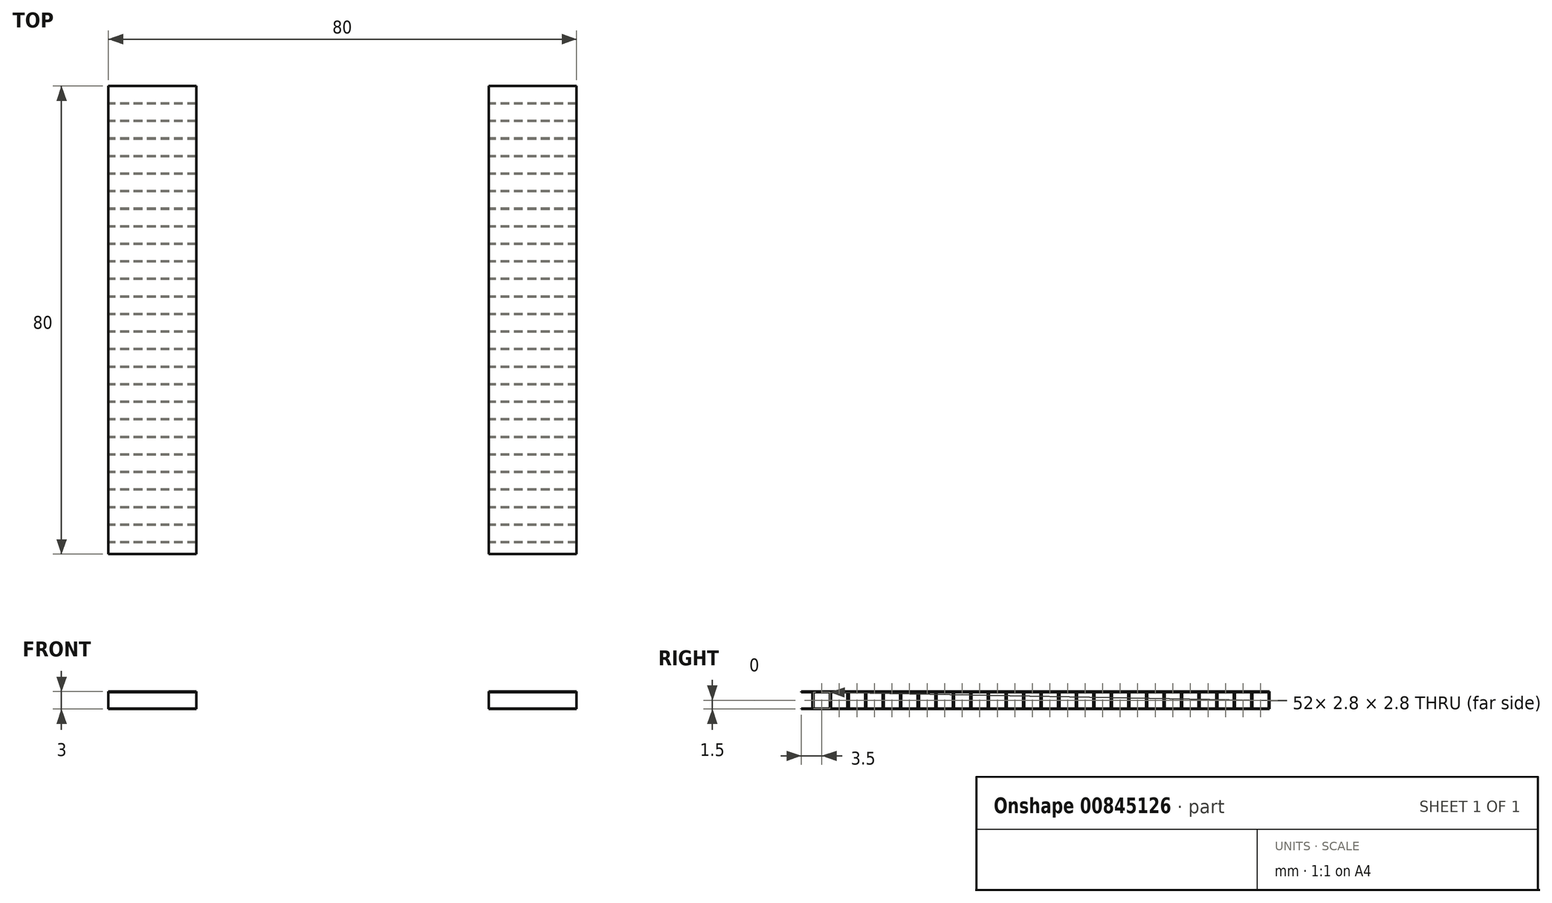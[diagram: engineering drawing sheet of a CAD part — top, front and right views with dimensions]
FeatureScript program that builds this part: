
annotation { "Feature Type Name" : "Feature", "Feature Type Description" : "" }
export const myFeature = defineFeature(function(context is Context, id is Id, definition is map)
    precondition{}
    {
        {
            var Q0;
            Q0=qCreatedBy(makeId("Top.planeOp"),FACE);
            var sketch = newSketch(context, id + "F0", { "sketchPlane" : qUnion([Q0])});
            skLineSegment(sketch, "E0.bottom", {"start": v(40, 40) * mm, "end": v(-40, 40) * mm});
            skLineSegment(sketch, "E0.top", {"start": v(40, -40) * mm, "end": v(-40, -40) * mm});
            skLineSegment(sketch, "E0.left", {"start": v(40, 40) * mm, "end": v(40, -40) * mm});
            skLineSegment(sketch, "E0.right", {"start": v(-40, 40) * mm, "end": v(-40, -40) * mm});
            skPoint(sketch, "E0.middle", {"position": v(0, 0) * mm});
            skLineSegment(sketch, "E1.bottom", {"start": v(-25, 40) * mm, "end": v(25, 40) * mm});
            skLineSegment(sketch, "E1.top", {"start": v(-25, -40) * mm, "end": v(25, -40) * mm});
            skLineSegment(sketch, "E1.left", {"start": v(-25, 40) * mm, "end": v(-25, -40) * mm});
            skLineSegment(sketch, "E1.right", {"start": v(25, 40) * mm, "end": v(25, -40) * mm});
            skSolve(sketch);
        }
        {
            var Q0;
            {var subQ0=sQuery(id+"F0.wireOp",EDGE,"E0.left");Q0=makeQuery(id+"F0.imprint","IMPRINT",FACE,{"disambiguationData":[TD([[makeQuery(id+"F0.imprint","IMPRINT",EDGE,{"derivedFrom":subQ0}),-1.0]])]});}
            var Q1;
            {var subQ0=sQuery(id+"F0.wireOp",EDGE,"E0.right");Q1=makeQuery(id+"F0.imprint","IMPRINT",FACE,{"disambiguationData":[TD([[makeQuery(id+"F0.imprint","IMPRINT",EDGE,{"derivedFrom":subQ0}),1.0]])]});}
            extrude(context, id + "F1", {"entities" : qUnion([Q0, Q1]), "depth" : 3 * mm, "offsetDistance" : 25 * mm});
        }
        {
            var Q0;
            Q0=makeQuery(id+"F1.opExtrude","SWEPT_FACE",FACE,{"disambiguationData":[OSD([sQuery(id+"F0.wireOp",EDGE,"E0.right")])]});
            var sketch = newSketch(context, id + "F2", { "sketchPlane" : qUnion([Q0])});
            skLineSegment(sketch, "E2.bottom", {"start": v(-39.9, 2.9) * mm, "end": v(39.9, 2.9) * mm});
            skLineSegment(sketch, "E2.top", {"start": v(-39.9, 0.1) * mm, "end": v(39.9, 0.1) * mm});
            skLineSegment(sketch, "E2.left", {"start": v(-39.9, 2.9) * mm, "end": v(-39.9, 0.1) * mm});
            skLineSegment(sketch, "E3", {"start": v(-37.1, 2.9) * mm, "end": v(-37.1, 0.1) * mm});
            skLineSegment(sketch, "E4.1.0.0", {"start": v(-36.9, 2.9) * mm, "end": v(-36.9, 0.1) * mm});
            skLineSegment(sketch, "E4.1.0.1", {"start": v(-34.1, 2.9) * mm, "end": v(-34.1, 0.1) * mm});
            skLineSegment(sketch, "E4.2.0.0", {"start": v(-33.9, 2.9) * mm, "end": v(-33.9, 0.1) * mm});
            skLineSegment(sketch, "E4.2.0.1", {"start": v(-31.1, 2.9) * mm, "end": v(-31.1, 0.1) * mm});
            skLineSegment(sketch, "E4.3.0.0", {"start": v(-30.9, 2.9) * mm, "end": v(-30.9, 0.1) * mm});
            skLineSegment(sketch, "E4.3.0.1", {"start": v(-28.1, 2.9) * mm, "end": v(-28.1, 0.1) * mm});
            skLineSegment(sketch, "E4.4.0.0", {"start": v(-27.9, 2.9) * mm, "end": v(-27.9, 0.1) * mm});
            skLineSegment(sketch, "E4.4.0.1", {"start": v(-25.1, 2.9) * mm, "end": v(-25.1, 0.1) * mm});
            skLineSegment(sketch, "E4.5.0.0", {"start": v(-24.9, 2.9) * mm, "end": v(-24.9, 0.1) * mm});
            skLineSegment(sketch, "E4.5.0.1", {"start": v(-22.1, 2.9) * mm, "end": v(-22.1, 0.1) * mm});
            skLineSegment(sketch, "E4.6.0.0", {"start": v(-21.9, 2.9) * mm, "end": v(-21.9, 0.1) * mm});
            skLineSegment(sketch, "E4.6.0.1", {"start": v(-19.1, 2.9) * mm, "end": v(-19.1, 0.1) * mm});
            skLineSegment(sketch, "E4.7.0.0", {"start": v(-18.9, 2.9) * mm, "end": v(-18.9, 0.1) * mm});
            skLineSegment(sketch, "E4.7.0.1", {"start": v(-16.1, 2.9) * mm, "end": v(-16.1, 0.1) * mm});
            skLineSegment(sketch, "E4.8.0.0", {"start": v(-15.9, 2.9) * mm, "end": v(-15.9, 0.1) * mm});
            skLineSegment(sketch, "E4.8.0.1", {"start": v(-13.1, 2.9) * mm, "end": v(-13.1, 0.1) * mm});
            skLineSegment(sketch, "E4.9.0.0", {"start": v(-12.9, 2.9) * mm, "end": v(-12.9, 0.1) * mm});
            skLineSegment(sketch, "E4.9.0.1", {"start": v(-10.1, 2.9) * mm, "end": v(-10.1, 0.1) * mm});
            skLineSegment(sketch, "E4.10.0.0", {"start": v(-9.9, 2.9) * mm, "end": v(-9.9, 0.1) * mm});
            skLineSegment(sketch, "E4.10.0.1", {"start": v(-7.1, 2.9) * mm, "end": v(-7.1, 0.1) * mm});
            skLineSegment(sketch, "E4.11.0.0", {"start": v(-6.9, 2.9) * mm, "end": v(-6.9, 0.1) * mm});
            skLineSegment(sketch, "E4.11.0.1", {"start": v(-4.1, 2.9) * mm, "end": v(-4.1, 0.1) * mm});
            skLineSegment(sketch, "E4.12.0.0", {"start": v(-3.9, 2.9) * mm, "end": v(-3.9, 0.1) * mm});
            skLineSegment(sketch, "E4.12.0.1", {"start": v(-1.1, 2.9) * mm, "end": v(-1.1, 0.1) * mm});
            skLineSegment(sketch, "E4.13.0.0", {"start": v(-0.9, 2.9) * mm, "end": v(-0.9, 0.1) * mm});
            skLineSegment(sketch, "E4.13.0.1", {"start": v(1.9, 2.9) * mm, "end": v(1.9, 0.1) * mm});
            skLineSegment(sketch, "E4.14.0.0", {"start": v(2.1, 2.9) * mm, "end": v(2.1, 0.1) * mm});
            skLineSegment(sketch, "E4.14.0.1", {"start": v(4.9, 2.9) * mm, "end": v(4.9, 0.1) * mm});
            skLineSegment(sketch, "E4.15.0.0", {"start": v(5.1, 2.9) * mm, "end": v(5.1, 0.1) * mm});
            skLineSegment(sketch, "E4.15.0.1", {"start": v(7.9, 2.9) * mm, "end": v(7.9, 0.1) * mm});
            skLineSegment(sketch, "E4.16.0.0", {"start": v(8.1, 2.9) * mm, "end": v(8.1, 0.1) * mm});
            skLineSegment(sketch, "E4.16.0.1", {"start": v(10.9, 2.9) * mm, "end": v(10.9, 0.1) * mm});
            skLineSegment(sketch, "E4.17.0.0", {"start": v(11.1, 2.9) * mm, "end": v(11.1, 0.1) * mm});
            skLineSegment(sketch, "E4.17.0.1", {"start": v(13.9, 2.9) * mm, "end": v(13.9, 0.1) * mm});
            skLineSegment(sketch, "E4.18.0.0", {"start": v(14.1, 2.9) * mm, "end": v(14.1, 0.1) * mm});
            skLineSegment(sketch, "E4.18.0.1", {"start": v(16.9, 2.9) * mm, "end": v(16.9, 0.1) * mm});
            skLineSegment(sketch, "E4.19.0.0", {"start": v(17.1, 2.9) * mm, "end": v(17.1, 0.1) * mm});
            skLineSegment(sketch, "E4.19.0.1", {"start": v(19.9, 2.9) * mm, "end": v(19.9, 0.1) * mm});
            skLineSegment(sketch, "E4.20.0.0", {"start": v(20.1, 2.9) * mm, "end": v(20.1, 0.1) * mm});
            skLineSegment(sketch, "E4.20.0.1", {"start": v(22.9, 2.9) * mm, "end": v(22.9, 0.1) * mm});
            skLineSegment(sketch, "E4.21.0.0", {"start": v(23.1, 2.9) * mm, "end": v(23.1, 0.1) * mm});
            skLineSegment(sketch, "E4.21.0.1", {"start": v(25.9, 2.9) * mm, "end": v(25.9, 0.1) * mm});
            skLineSegment(sketch, "E4.22.0.0", {"start": v(26.1, 2.9) * mm, "end": v(26.1, 0.1) * mm});
            skLineSegment(sketch, "E4.22.0.1", {"start": v(28.9, 2.9) * mm, "end": v(28.9, 0.1) * mm});
            skLineSegment(sketch, "E4.23.0.0", {"start": v(29.1, 2.9) * mm, "end": v(29.1, 0.1) * mm});
            skLineSegment(sketch, "E4.23.0.1", {"start": v(31.9, 2.9) * mm, "end": v(31.9, 0.1) * mm});
            skLineSegment(sketch, "E4.24.0.0", {"start": v(32.1, 2.9) * mm, "end": v(32.1, 0.1) * mm});
            skLineSegment(sketch, "E4.24.0.1", {"start": v(34.9, 2.9) * mm, "end": v(34.9, 0.1) * mm});
            skLineSegment(sketch, "E4.25.0.0", {"start": v(35.1, 2.9) * mm, "end": v(35.1, 0.1) * mm});
            skLineSegment(sketch, "E4.25.0.1", {"start": v(37.9, 2.9) * mm, "end": v(37.9, 0.1) * mm});
            skLineSegment(sketch, "E4.26.0.0", {"start": v(38.1, 2.9) * mm, "end": v(38.1, 0.1) * mm});
            skLineSegment(sketch, "E4.26.0.1", {"start": v(40.9, 2.9) * mm, "end": v(40.9, 0.1) * mm});
            skLineSegment(sketch, "E4.direction1", {"start": v(-39.9, 0.1) * mm, "end": v(-36.9, 0.1) * mm, "construction": true});
            skLineSegment(sketch, "E5", {"start": v(39.9, 2.9) * mm, "end": v(40.9, 2.9) * mm});
            skLineSegment(sketch, "E6", {"start": v(39.9, 0.1) * mm, "end": v(40.9, 0.1) * mm});
            skSolve(sketch);
        }
        {
            var Q0;
            {var subQ0=sQuery(id+"F2.wireOp",EDGE,"E4.1.0.0");Q0=makeQuery(id+"F2.imprint","IMPRINT",FACE,{"disambiguationData":[TD([[makeQuery(id+"F2.imprint","IMPRINT",EDGE,{"derivedFrom":subQ0}),1.0]])]});}
            var Q1;
            {var subQ0=sQuery(id+"F2.wireOp",EDGE,"E4.2.0.0");Q1=makeQuery(id+"F2.imprint","IMPRINT",FACE,{"disambiguationData":[TD([[makeQuery(id+"F2.imprint","IMPRINT",EDGE,{"derivedFrom":subQ0}),1.0]])]});}
            var Q2;
            {var subQ0=sQuery(id+"F2.wireOp",EDGE,"E4.3.0.0");Q2=makeQuery(id+"F2.imprint","IMPRINT",FACE,{"disambiguationData":[TD([[makeQuery(id+"F2.imprint","IMPRINT",EDGE,{"derivedFrom":subQ0}),1.0]])]});}
            var Q3;
            {var subQ0=sQuery(id+"F2.wireOp",EDGE,"E4.4.0.0");Q3=makeQuery(id+"F2.imprint","IMPRINT",FACE,{"disambiguationData":[TD([[makeQuery(id+"F2.imprint","IMPRINT",EDGE,{"derivedFrom":subQ0}),1.0]])]});}
            var Q4;
            {var subQ0=sQuery(id+"F2.wireOp",EDGE,"E4.5.0.0");Q4=makeQuery(id+"F2.imprint","IMPRINT",FACE,{"disambiguationData":[TD([[makeQuery(id+"F2.imprint","IMPRINT",EDGE,{"derivedFrom":subQ0}),1.0]])]});}
            var Q5;
            {var subQ0=sQuery(id+"F2.wireOp",EDGE,"E4.6.0.0");Q5=makeQuery(id+"F2.imprint","IMPRINT",FACE,{"disambiguationData":[TD([[makeQuery(id+"F2.imprint","IMPRINT",EDGE,{"derivedFrom":subQ0}),1.0]])]});}
            var Q6;
            {var subQ0=sQuery(id+"F2.wireOp",EDGE,"E4.7.0.0");Q6=makeQuery(id+"F2.imprint","IMPRINT",FACE,{"disambiguationData":[TD([[makeQuery(id+"F2.imprint","IMPRINT",EDGE,{"derivedFrom":subQ0}),1.0]])]});}
            var Q7;
            {var subQ0=sQuery(id+"F2.wireOp",EDGE,"E4.8.0.0");Q7=makeQuery(id+"F2.imprint","IMPRINT",FACE,{"disambiguationData":[TD([[makeQuery(id+"F2.imprint","IMPRINT",EDGE,{"derivedFrom":subQ0}),1.0]])]});}
            var Q8;
            {var subQ0=sQuery(id+"F2.wireOp",EDGE,"E4.9.0.0");Q8=makeQuery(id+"F2.imprint","IMPRINT",FACE,{"disambiguationData":[TD([[makeQuery(id+"F2.imprint","IMPRINT",EDGE,{"derivedFrom":subQ0}),1.0]])]});}
            var Q9;
            {var subQ0=sQuery(id+"F2.wireOp",EDGE,"E4.10.0.0");Q9=makeQuery(id+"F2.imprint","IMPRINT",FACE,{"disambiguationData":[TD([[makeQuery(id+"F2.imprint","IMPRINT",EDGE,{"derivedFrom":subQ0}),1.0]])]});}
            var Q10;
            {var subQ0=sQuery(id+"F2.wireOp",EDGE,"E4.11.0.0");Q10=makeQuery(id+"F2.imprint","IMPRINT",FACE,{"disambiguationData":[TD([[makeQuery(id+"F2.imprint","IMPRINT",EDGE,{"derivedFrom":subQ0}),1.0]])]});}
            var Q11;
            {var subQ0=sQuery(id+"F2.wireOp",EDGE,"E4.12.0.0");Q11=makeQuery(id+"F2.imprint","IMPRINT",FACE,{"disambiguationData":[TD([[makeQuery(id+"F2.imprint","IMPRINT",EDGE,{"derivedFrom":subQ0}),1.0]])]});}
            var Q12;
            {var subQ0=sQuery(id+"F2.wireOp",EDGE,"E4.13.0.0");Q12=makeQuery(id+"F2.imprint","IMPRINT",FACE,{"disambiguationData":[TD([[makeQuery(id+"F2.imprint","IMPRINT",EDGE,{"derivedFrom":subQ0}),1.0]])]});}
            var Q13;
            {var subQ0=sQuery(id+"F2.wireOp",EDGE,"E4.14.0.0");Q13=makeQuery(id+"F2.imprint","IMPRINT",FACE,{"disambiguationData":[TD([[makeQuery(id+"F2.imprint","IMPRINT",EDGE,{"derivedFrom":subQ0}),1.0]])]});}
            var Q14;
            {var subQ0=sQuery(id+"F2.wireOp",EDGE,"E4.15.0.0");Q14=makeQuery(id+"F2.imprint","IMPRINT",FACE,{"disambiguationData":[TD([[makeQuery(id+"F2.imprint","IMPRINT",EDGE,{"derivedFrom":subQ0}),1.0]])]});}
            var Q15;
            {var subQ0=sQuery(id+"F2.wireOp",EDGE,"E4.17.0.0");Q15=makeQuery(id+"F2.imprint","IMPRINT",FACE,{"disambiguationData":[TD([[makeQuery(id+"F2.imprint","IMPRINT",EDGE,{"derivedFrom":subQ0}),1.0]])]});}
            var Q16;
            {var subQ0=sQuery(id+"F2.wireOp",EDGE,"E4.18.0.0");Q16=makeQuery(id+"F2.imprint","IMPRINT",FACE,{"disambiguationData":[TD([[makeQuery(id+"F2.imprint","IMPRINT",EDGE,{"derivedFrom":subQ0}),1.0]])]});}
            var Q17;
            {var subQ0=sQuery(id+"F2.wireOp",EDGE,"E4.19.0.0");Q17=makeQuery(id+"F2.imprint","IMPRINT",FACE,{"disambiguationData":[TD([[makeQuery(id+"F2.imprint","IMPRINT",EDGE,{"derivedFrom":subQ0}),1.0]])]});}
            var Q18;
            {var subQ0=sQuery(id+"F2.wireOp",EDGE,"E4.20.0.0");Q18=makeQuery(id+"F2.imprint","IMPRINT",FACE,{"disambiguationData":[TD([[makeQuery(id+"F2.imprint","IMPRINT",EDGE,{"derivedFrom":subQ0}),1.0]])]});}
            var Q19;
            {var subQ0=sQuery(id+"F2.wireOp",EDGE,"E4.21.0.0");Q19=makeQuery(id+"F2.imprint","IMPRINT",FACE,{"disambiguationData":[TD([[makeQuery(id+"F2.imprint","IMPRINT",EDGE,{"derivedFrom":subQ0}),1.0]])]});}
            var Q20;
            {var subQ0=sQuery(id+"F2.wireOp",EDGE,"E4.22.0.0");Q20=makeQuery(id+"F2.imprint","IMPRINT",FACE,{"disambiguationData":[TD([[makeQuery(id+"F2.imprint","IMPRINT",EDGE,{"derivedFrom":subQ0}),1.0]])]});}
            var Q21;
            {var subQ0=sQuery(id+"F2.wireOp",EDGE,"E4.23.0.0");Q21=makeQuery(id+"F2.imprint","IMPRINT",FACE,{"disambiguationData":[TD([[makeQuery(id+"F2.imprint","IMPRINT",EDGE,{"derivedFrom":subQ0}),1.0]])]});}
            var Q22;
            {var subQ0=sQuery(id+"F2.wireOp",EDGE,"E4.24.0.0");Q22=makeQuery(id+"F2.imprint","IMPRINT",FACE,{"disambiguationData":[TD([[makeQuery(id+"F2.imprint","IMPRINT",EDGE,{"derivedFrom":subQ0}),1.0]])]});}
            var Q23;
            {var subQ0=sQuery(id+"F2.wireOp",EDGE,"E4.25.0.0");Q23=makeQuery(id+"F2.imprint","IMPRINT",FACE,{"disambiguationData":[TD([[makeQuery(id+"F2.imprint","IMPRINT",EDGE,{"derivedFrom":subQ0}),1.0]])]});}
            var Q24;
            {var subQ0=sQuery(id+"F2.wireOp",EDGE,"E4.26.0.1");Q24=makeQuery(id+"F2.imprint","IMPRINT",FACE,{"disambiguationData":[TD([[makeQuery(id+"F2.imprint","IMPRINT",EDGE,{"derivedFrom":subQ0}),-1.0]])]});}
            var Q25;
            {var subQ0=sQuery(id+"F2.wireOp",EDGE,"E4.26.0.0");Q25=makeQuery(id+"F2.imprint","IMPRINT",FACE,{"disambiguationData":[TD([[makeQuery(id+"F2.imprint","IMPRINT",EDGE,{"derivedFrom":subQ0}),1.0]])]});}
            var Q26;
            {var subQ0=sQuery(id+"F2.wireOp",EDGE,"E2.left");Q26=makeQuery(id+"F2.imprint","IMPRINT",FACE,{"disambiguationData":[TD([[makeQuery(id+"F2.imprint","IMPRINT",EDGE,{"derivedFrom":subQ0}),1.0]])]});}
            var Q27;
            {var subQ0=sQuery(id+"F2.wireOp",EDGE,"E4.16.0.0");Q27=makeQuery(id+"F2.imprint","IMPRINT",FACE,{"disambiguationData":[TD([[makeQuery(id+"F2.imprint","IMPRINT",EDGE,{"derivedFrom":subQ0}),1.0]])]});}
            extrude(context, id + "F3", {"entities" : qUnion([Q0, Q1, Q2, Q3, Q4, Q5, Q6, Q7, Q8, Q9, Q10, Q11, Q12, Q13, Q14, Q15, Q16, Q17, Q18, Q19, Q20, Q21, Q22, Q23, Q24, Q25, Q26, Q27]), "operationType" : NewBodyOperationType.REMOVE, "oppositeDirection" : true, "depth" : 80 * mm, "offsetDistance" : 25 * mm});
        }
    });
